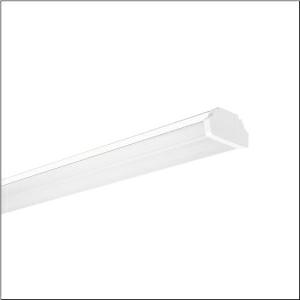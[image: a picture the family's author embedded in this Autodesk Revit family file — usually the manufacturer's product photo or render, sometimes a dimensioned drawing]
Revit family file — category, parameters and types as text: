
# Revit family: modario_31_gen_2_53bm812mv4g5d2_cdf0
name_source: partatom
category: Lighting Fixtures
units: mm (PartAtom-declared; Revit-internal decimal feet)

## family parameters
Cut with Voids When Loaded = No
Host = Face
Light Source = No
Part Type = Normal
Room Calculation Point = No
Round Connector Dimension = Use Diameter
Shared = No

## types (1)
- --- (1 x LED, 16690 lm, 89.8 W, 4000K)
    Apparent Load = 90 VA
    CIE Flux Codes = 47 80 95 93 100
    Color Rendering = 80
    Color Temperature = 4000K
    Default Elevation = 1800 mm
    Description = Modario 31 Gen.2, luminaire insert, of sheet steel, coil coated, white, length: 1.495mm, width: 81mm, height: 82mm, 5x system unit, system units: 299mm, LED rated luminous flux: 16.690lm, light colour: 840, SDCM (Standard Deviation of Colour Matching)MacAdam ≤ 3 SDCM (initial), control gear: ON/OFF Multilumen, control gear: ECG, with plug, 3-pole, with phase selection, mains connection: 220..240V, AC, 50/60Hz, rated input power: 90W, through-wiring accessed according to module size, primary optical cover: cover, of PMMA, light emission: direct distribution, primary light characteristic: symmetric, protection rating (complete): IP20, protection rating (LED compartment): IP50, insulation class (complete): insulation class I (protective earthing), certification: CE, ENEC, VDE, UKCA, impact resistance: IK03, permissible ambient temperature for indoor applications: -35..+30°C, corresponds to IFS (International Featured Standards) requirements for safety and quality in the food industry, reducing of maximum allowable ambient temperature of 5°C with ceiling mounting, IP40 when using the optional accessory 5TP9018, packaging unit: 1 piece
    Height = 92 mm
    Lamp = 1 x LED
    Lamp Light Flux = 16690 lm
    Lamp Power = 89.8 W
    Lamp count = 1
    Length = 1495 mm
    Luminous efficacy = 186 lm/W
    Manufacturer = Siteco
    ModVariant = No
    Model = 53BM812MV4G5D2
    Mounting Place = Ceiling
    Mounting Type = Pendant
    Number of Poles = 1
    OnlyDefault = Yes
    Power Factor = 1
    Product Name = Modario 31 Gen.2
    Product group = luminaire insert | ceiling pendant
    ProductGroupID = 901
    Protection Class = Protection class I
    Protection Degree = IP 20
    RLX_Detail_Level = 1
    RLX_Emergency_Light_Flux = 0 lm
    RLX_Emergency_Type = 0
    RLX_Emergency_Type_DB = No
    RlxData = <blob elided: 39817 chars, md5=d5fcb6b7>
    Socket = socket
    Standby Power = 0 W
    System Light Flux = 16690 lm
    System Power = 90 W
    Type Comments = factory setting: luminous flux: 100 % | (A | C | E) | 210 mA
    Type Image = l_1341886.jpg
    URL = http://relux.com
    VarID = @adj_052363
    Voltage = 0 V
    Weight = 0.00 kg
    Width = 81 mm

## geometry (parser evidence)
native form markers: Blend x4, Sweep x12
no freeform markers — native parametric forms only
